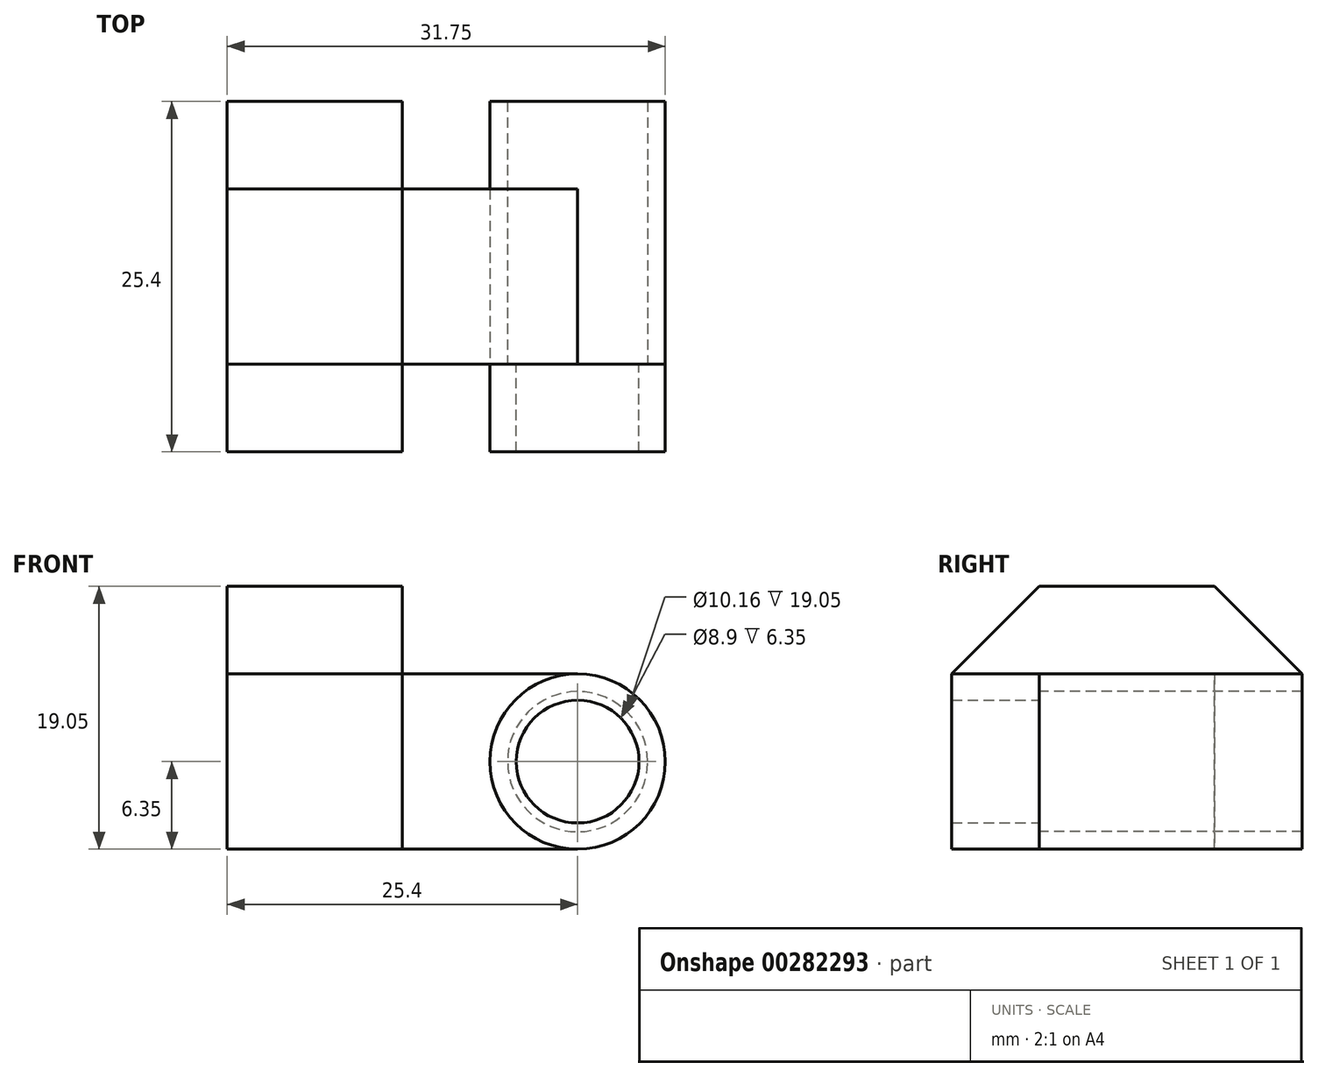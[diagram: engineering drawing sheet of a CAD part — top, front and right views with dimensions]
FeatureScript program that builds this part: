
annotation { "Feature Type Name" : "Feature", "Feature Type Description" : "" }
export const myFeature = defineFeature(function(context is Context, id is Id, definition is map)
    precondition{}
    {
        {
            var Q0;
            Q0=qCreatedBy(makeId("Front.planeOp"),FACE);
            var sketch = newSketch(context, id + "F0", { "sketchPlane" : qUnion([Q0])});
            skLineSegment(sketch, "E0.bottom", {"start": v(0, 0) * mm, "end": v(-12.7, 0) * mm});
            skLineSegment(sketch, "E0.top", {"start": v(0, 12.7) * mm, "end": v(-12.7, 12.7) * mm});
            skLineSegment(sketch, "E0.right", {"start": v(-12.7, 0) * mm, "end": v(-12.7, 12.7) * mm});
            skArc(sketch, "E1", {"start": v(0, 12.7) * mm, "mid": v(-6.35, 6.35) * mm, "end": v(0, 0) * mm});
            skPoint(sketch, "E1.midSnap0", {"position": v(0, 6.35) * mm});
            skPoint(sketch, "E1.midSnap1", {"position": v(-6.35, 12.7) * mm});
            skSolve(sketch);
        }
        {
            var Q0;
            Q0 = qSketchRegion(id + "F0", true);
            extrude(context, id + "F1", {"entities" : qUnion([Q0]), "depth" : 12.7 * mm});
        }
        {
            var Q0;
            Q0=makeQuery(id+"F1.opExtrude","CAP_FACE",FACE,{"disambiguationData":[OSD([sQuery(id+"F0.wireOp",EDGE,"E0.bottom"),sQuery(id+"F0.wireOp",EDGE,"E0.top"),sQuery(id+"F0.wireOp",EDGE,"E0.left"),sQuery(id+"F0.wireOp",EDGE,"E0.right")])],"isStart":false});
            var sketch = newSketch(context, id + "F2", { "sketchPlane" : qUnion([Q0])});
            skCircle(sketch, "E2", {"center": v(0, 6.35) * mm, "radius": 6.35 * mm});
            skCircle(sketch, "E3", {"center": v(0, 6.35) * mm, "radius": 4.45 * mm});
            skSolve(sketch);
        }
        {
            var Q0;
            Q0 = qSketchRegion(id + "F2", true);
            extrude(context, id + "F3", {"entities" : qUnion([Q0]), "depth" : 6.35 * mm});
        }
        {
            var Q0;
            Q0=makeQuery(id+"F3.opExtrude","CAP_FACE",FACE,{"disambiguationData":[OSD([sQuery(id+"F2.wireOp",EDGE,"E2"),sQuery(id+"F2.wireOp",EDGE,"E3")])],"isStart":true});
            var sketch = newSketch(context, id + "F4", { "sketchPlane" : qUnion([Q0])});
            skCircle(sketch, "E4", {"center": v(0, 6.35) * mm, "radius": 6.35 * mm});
            skCircle(sketch, "E5", {"center": v(0, 6.35) * mm, "radius": 5.08 * mm});
            skSolve(sketch);
        }
        {
            var Q0;
            Q0 = qSketchRegion(id + "F4", true);
            extrude(context, id + "F5", {"entities" : qUnion([Q0]), "depth" : 19.05 * mm});
        }
        {
            var Q0;
            Q0=makeQuery(id+"F1.opExtrude","SWEPT_FACE",FACE,{"disambiguationData":[OSD([sQuery(id+"F0.wireOp",EDGE,"E0.right")])]});
            var sketch = newSketch(context, id + "F6", { "sketchPlane" : qUnion([Q0])});
            skLineSegment(sketch, "E6", {"start": v(0, 19.05) * mm, "end": v(12.7, 19.05) * mm});
            skLineSegment(sketch, "E7", {"start": v(12.7, 19.05) * mm, "end": v(19.05, 12.7) * mm});
            skLineSegment(sketch, "E8", {"start": v(19.05, 12.7) * mm, "end": v(19.05, 0) * mm});
            skLineSegment(sketch, "E9", {"start": v(19.05, 0) * mm, "end": v(-6.35, 0) * mm});
            skLineSegment(sketch, "E10", {"start": v(-6.35, 0) * mm, "end": v(-6.35, 12.7) * mm});
            skLineSegment(sketch, "E11", {"start": v(-6.35, 12.7) * mm, "end": v(0, 19.05) * mm});
            skSolve(sketch);
        }
        {
            var Q0;
            Q0 = qSketchRegion(id + "F6", true);
            extrude(context, id + "F7", {"entities" : qUnion([Q0]), "operationType" : NewBodyOperationType.ADD, "depth" : 12.7 * mm});
        }
    });
